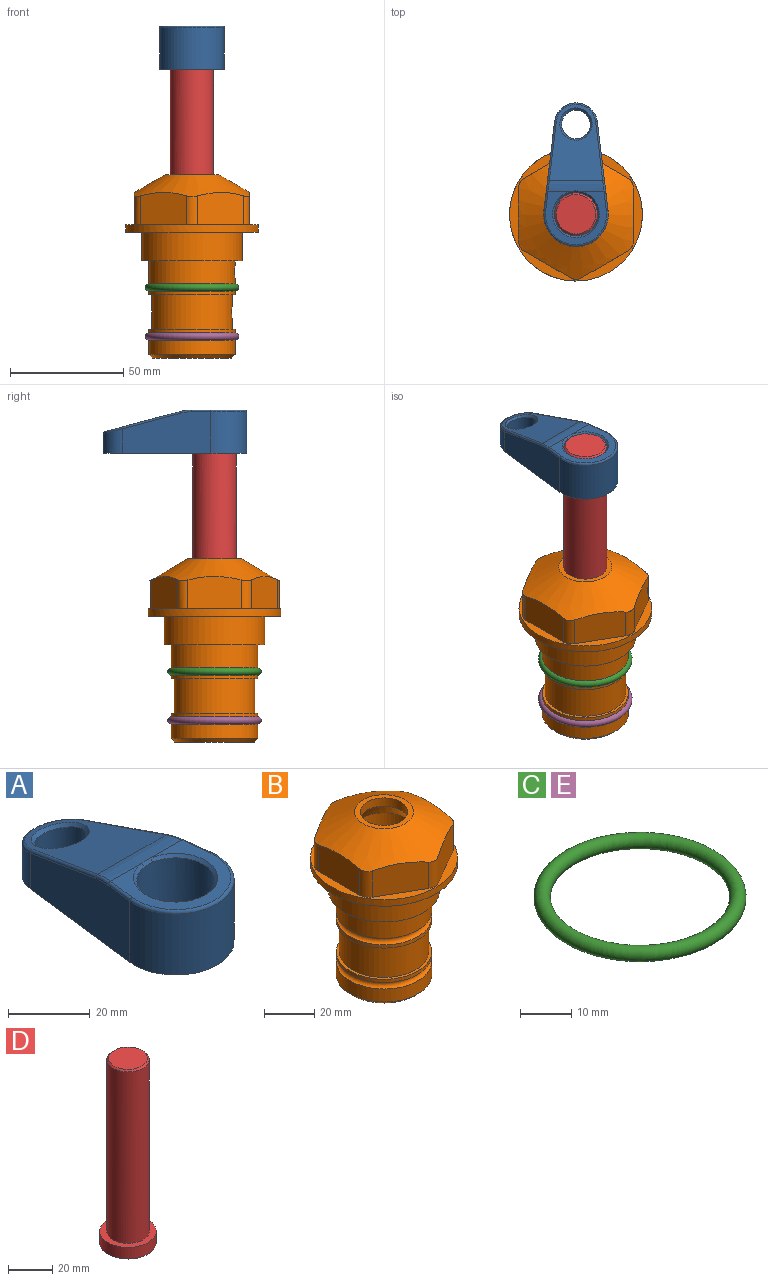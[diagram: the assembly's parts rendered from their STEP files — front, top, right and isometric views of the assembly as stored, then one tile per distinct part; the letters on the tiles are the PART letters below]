
ASSEMBLY  parts=5 mates=4
PART A: 31 faces, bbox 31.7x65.5x19.8 mm
  f0: plane 39.12x18.26mm, normal (0.99,0.12,0), area 612.2mm2, adj f1,f4,f7,f11,f13,f15
  f1: cylinder r=9.53mm len=18.91mm, axis (0,0,-1), area 296.1mm2, adj f0,f2,f7,f17
  f2: plane 39.12x18.26mm, normal (-0.99,0.12,0), area 612.2mm2, adj f1,f4,f7,f12,f14,f16
  f3: cylinder r=6.35mm len=12.7mm, axis (0,0,-1), area 362.4mm2, adj f7,f18
  f4: cylinder r=14.29mm len=28.58mm, axis (0,0,-1), area 882.2mm2, adj f0,f2,f7,f10
  f5: cylinder r=9.53mm len=19.05mm, axis (0,0,-1), area 1092.6mm2, adj f7,f19,f20
  f6: plane 26.99x23.69mm, normal (0,0,1), area 216.2mm2, adj f9,f10,f11,f12,f19
  f7: plane 63.5x28.58mm, normal (0,0,-1), area 661.8mm2, adj f0,f1,f2,f3,f4,f5,f22,f23
  f8: plane 33.52x23.6mm, normal (0,0.26,0.97), area 486mm2, adj f9,f15,f16,f17,f18
  f9: cylinder r=19.05mm len=24.72mm, axis (1,0,0), area 120.4mm2, adj f6,f8,f13,f14,f20
  f10: torus R=13.49mm, axis (0,0,1), area 59mm2, adj f4,f6,f11,f12
  f11: cylinder r=0.79mm len=8.67mm, axis (0.12,-0.99,0), area 10.8mm2, adj f0,f6,f10,f13
  f12: cylinder r=0.79mm len=8.67mm, axis (0.12,0.99,0), area 10.8mm2, adj f2,f6,f10,f14
  f13: bspline ~4.95x1.42mm, area 6.1mm2, adj f0,f9,f11,f15
  f14: bspline ~4.95x1.42mm, area 6.1mm2, adj f2,f9,f12,f16
  f15: cylinder r=0.79mm len=25.95mm, axis (0.12,-0.96,0.26), area 32.9mm2, adj f0,f8,f13,f17
  f16: cylinder r=0.79mm len=25.95mm, axis (0.12,0.96,-0.26), area 32.9mm2, adj f2,f8,f14,f17
  f17: bspline ~18.91x8.38mm, area 30mm2, adj f1,f8,f15,f16
  f18: bspline ~14.29x14.29mm, area 48.3mm2, adj f3,f8
  f19: cone r=9.53mm half-angle=45deg, axis (0,0,1), area 66.5mm2, adj f5,f6,f20
  f20: bspline ~3.22x0.96mm, area 3.5mm2, adj f5,f9,f19
  f21: plane 2.75x2.72mm, normal (0,0,-1), area 2.9mm2, adj f23,f25,f28
  f22: plane 23.05x15.88mm, normal (-0.99,-0.12,0), area 323.6mm2, adj f7,f25,f26,f27,f28,f29
  f23: plane 23.05x15.88mm, normal (0.99,-0.12,0), area 323.6mm2, adj f7,f21,f25,f27,f28,f30
  f24: cylinder r=9.53mm len=10.69mm, axis (0,0,-1), area 114.7mm2, adj f7,f27,f29,f30
  f25: cylinder r=12.7mm len=20.59mm, axis (0,0,-1), area 381.1mm2, adj f7,f21,f22,f23,f26,f28
  f26: plane 2.75x2.72mm, normal (0,0,-1), area 2.9mm2, adj f22,f25,f28
  f27: plane 19.72x18.37mm, normal (0,-0.26,-0.97), area 291.8mm2, adj f22,f23,f24,f28,f29,f30
  f28: cylinder r=15.88mm len=19.92mm, axis (1,0,0), area 54.8mm2, adj f21,f22,f23,f25,f26,f27
  f29: cylinder r=1.59mm len=11mm, axis (0,0,-1), area 34.7mm2, adj f7,f22,f24,f27
  f30: cylinder r=1.59mm len=11mm, axis (0,0,-1), area 34.7mm2, adj f7,f23,f24,f27
PART B: 36 faces, bbox 58.7x58.7x81 mm
  f0: cylinder r=17.78mm len=35.56mm, axis (0,0,1), area 1670.8mm2, adj f23,f24,f31
  f1: cylinder r=19.05mm len=38.1mm, axis (0,0,1), area 1191.9mm2, adj f26,f27,f30
  f2: plane 58.66x58.66mm, normal (0,0,-1), area 1150.6mm2, adj f3,f28
  f3: cylinder r=29.33mm len=58.66mm, axis (0,0,-1), area 585.1mm2, adj f2,f4
  f4: plane 58.66x58.66mm, normal (0,0,1), area 475.9mm2, adj f3,f5,f6,f7,f8,f9,f10,f11
  f5: plane 20.32x14.34mm, normal (-0.5,0.87,0), area 324.4mm2, adj f4,f15,f16,f17
  f6: plane 20.32x14.34mm, normal (0.5,0.87,0), area 324.4mm2, adj f4,f14,f15,f17
  f7: plane 23.48x14.34mm, normal (1,0,0), area 324.4mm2, adj f4,f13,f14,f17
  f8: plane 20.32x14.34mm, normal (0.5,-0.87,0), area 324.4mm2, adj f4,f12,f13,f17
  f9: plane 20.32x14.34mm, normal (-0.5,-0.87,0), area 324.4mm2, adj f4,f11,f12,f17
  f10: plane 23.48x14.34mm, normal (-1,0,0), area 324.4mm2, adj f4,f11,f16,f17
  f11: cylinder r=5.08mm len=12.85mm, axis (0,0,-1), area 67.2mm2, adj f4,f9,f10,f17
  f12: cylinder r=5.08mm len=12.85mm, axis (0,0,-1), area 67.2mm2, adj f4,f8,f9,f17
  f13: cylinder r=5.08mm len=12.85mm, axis (0,0,-1), area 67.2mm2, adj f4,f7,f8,f17
  f14: cylinder r=5.08mm len=12.85mm, axis (0,0,-1), area 67.2mm2, adj f4,f6,f7,f17
  f15: cylinder r=5.08mm len=12.85mm, axis (0,0,-1), area 67.2mm2, adj f4,f5,f6,f17
  f16: cylinder r=5.08mm len=12.85mm, axis (0,0,-1), area 67.2mm2, adj f4,f5,f10,f17
  f17: cone r=11.73mm half-angle=60deg, axis (0,0,-1), area 2071.8mm2, adj f5,f6,f7,f8,f9,f10,f11,f12
  f18: plane 23.46x23.46mm, normal (0,0,1), area 147.4mm2, adj f17,f35
  f19: plane 34.93x34.93mm, normal (0,0,-1), area 958mm2, adj f29
  f20: cylinder r=19.05mm len=38.1mm, axis (0,0,1), area 760.1mm2, adj f21,f29
  f21: torus R=19.05mm, axis (0,0,1), area 565.3mm2, adj f20,f22
  f22: cylinder r=19.05mm len=38.1mm, axis (0,0,1), area 190mm2, adj f21,f23
  f23: plane 38.1x38.1mm, normal (0,0,1), area 146.9mm2, adj f0,f22
  f24: plane 38.1x38.1mm, normal (0,0,-1), area 146.9mm2, adj f0,f25
  f25: cylinder r=19.05mm len=38.1mm, axis (0,0,1), area 190mm2, adj f24,f26
  f26: torus R=19.05mm, axis (0,0,1), area 565.3mm2, adj f1,f25
  f27: plane 44.45x44.45mm, normal (0,0,-1), area 411.7mm2, adj f1,f28
  f28: cylinder r=22.23mm len=44.45mm, axis (0,0,1), area 1773.5mm2, adj f2,f27
  f29: cone r=19.05mm half-angle=45deg, axis (0,0,1), area 257.5mm2, adj f19,f20
  f30: cylinder r=3.17mm len=6.75mm, axis (-1,0,0), area 128mm2, adj f1,f33
  f31: cylinder r=3.17mm len=6.35mm, axis (-1,0,0), area 102.5mm2, adj f0,f33
  f32: plane 25.4x25.4mm, normal (0,0,1), area 506.7mm2, adj f33
  f33: cylinder r=12.7mm len=66.42mm, axis (0,0,-1), area 5236.2mm2, adj f30,f31,f32,f34
  f34: cone r=9.53mm half-angle=30deg, axis (0,0,-1), area 443.4mm2, adj f33,f35
  f35: cylinder r=9.53mm len=19.05mm, axis (0,0,-1), area 240.9mm2, adj f18,f34
PART C: 1 faces, bbox 44.7x44.7x3.2 mm
  f0: torus R=19.05mm, axis (0,0,1), area 1193.9mm2
PART D: 6 faces, bbox 25.4x25.4x101.6 mm
  f0: plane 17.46x17.46mm, normal (0,0,1), area 239.5mm2, adj f5
  f1: plane 25.4x25.4mm, normal (0,0,-1), area 506.7mm2, adj f2
  f2: cylinder r=12.7mm len=25.4mm, axis (0,0,1), area 506.7mm2, adj f1,f3
  f3: plane 25.4x25.4mm, normal (0,0,1), area 221.7mm2, adj f2,f4
  f4: cylinder r=9.53mm len=94.46mm, axis (0,0,1), area 5653mm2, adj f3,f5
  f5: cone r=8.73mm half-angle=45deg, axis (0,0,-1), area 64.4mm2, adj f0,f4
PART E: same geometry as C
PLACE A t=(0,0,27.55)mm
PLACE B at identity fixed
PLACE C at identity
PLACE D t=(0,0,27.55)mm
PLACE E t=(0,0,-21.59)mm
MATE fastened E.f0 <-> B.f0  axis (0,0,1) through (0,0,-46.1)mm
MATE fastened C.f0 <-> B.f0  axis (0,0,1) through (0,0,-24.51)mm
MATE fastened A.f4 <-> D.f2  axis (0,0,1) through (0,0,91.05)mm
MATE cylindrical D.f2 <-> B.f0  axis (0,0,-1) through (0,0,-10.55)mm
